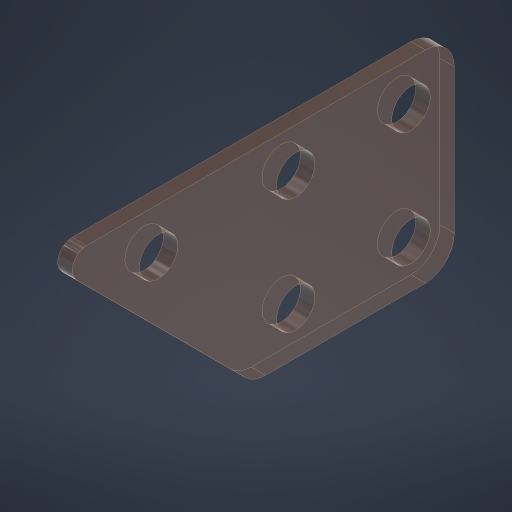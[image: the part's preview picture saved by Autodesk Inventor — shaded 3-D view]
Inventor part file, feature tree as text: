
AUTODESK INVENTOR PART (.ipt)
format: ipt  version: 2024 (Build 280153000, 153)  size: 253,952 bytes
history: native  units: in
note: dims shown in document units (in); Inventor stores cm internally (conversion verified against a paired STEP export)
features: sketch x3, extrude x1, hole x1, split x1
ambient origin geometry x8: Origin, YZ Plane, XZ Plane, XY Plane, X Axis, Y Axis, Z Axis, Center Point
bodies: Solid1 (feature_tree)
feature tree (6):
  extrude  "Extrusion1"  Depth=0.125in
  hole  "Hole1"  [1 undecoded]
  split  "Split1"
  sketch  "Sketch1"  dims[d1=0.875in d6=0.125in]
  sketch  "Sketch2"  dims[d7=0.0625in d8=0.0in d13=0.1875in]
  sketch  "Sketch3"  dims[d14=0.5in d15=0.25in d16=0.5in d17=0.167in d18=0.75in d19=0.375in d20=0.25in d21=0.5635in d22=1.0in d23=0.8108in d46=0.0625in d47=0.125in d49=0.188in d50=45.0deg d51=0.403in d52=45.0deg]
note: 1 required parameter value undecoded (feature->parameter linkage not recoverable at this tier; creation-order binding heuristic only, values carry confidence <= 0.55)
